# Revit family: Krill 3.4
name_source: partatom
category: Lighting Fixtures
units: mm (PartAtom-declared; Revit-internal decimal feet)

## family parameters
Always vertical = No
Cut with Voids When Loaded = No
Light Source = No
OmniClass Number = 23.80.70.00
OmniClass Title = Lighting
Part Type = Normal
Room Calculation Point = Yes
Round Connector Dimension = Use Diameter
Shared = No
Work Plane-Based = No

## types (2) — shared parameters
Apparent Load Phase 1 = 5 W
Base = L&L_Anticorodal aluminium
Base bracket = Krill 1.4_Base braket
Body = L&L_Anticorodal aluminium
CRI = CRI>90
Code = -
Control system = -
Cutout dimensions = -
Delivered lumen output = 253 lm (3000K, 350mA, 80°)
Description = Projectors for indoor applications
Energy efficiency class = A A+ A++
Features = -
Geometry = Krill 3.4_mod
H1 = 16 mm  [stored 0.0524934 ft]
IP = IP40
Joint = L&L_Brass
LED Colour = 3000K (also available: 2700, 4000K - ref. URL Technical sheet)
Length mm = 40 mm  [stored 0.131234 ft]
Lens = L&L_Tempered extra-clear glass
Lumen output at source = 452 lm (3000K, 350mA)
Manufacturer = L&L Luce&Light
Material = body in anticorodal aluminium, joint in brass
Model = Krill 3.4
Mounting = surface mounted (shop windows, display cabinets)
No. and type of led = 1 power LED High Intensity, 3-step MacAdam, 50 000h L90 B10 (Ta 25°C)
Notes = -
Power = max 4.5W
Power cables = includes 1.5 m PVC cable HT105° 2x0.20 Ø3.0 mm
Power supply = max 350mA
Power supply unit = not included
not included
not included
Trim = L&L_Black aluminium
URL = https://www.lucelight.it
URL Accessories and power supply units = https://www.lucelight.it
URL Catalogue = -
URL DXF = https://www.lucelight.it
URL Description = https://www.lucelight.it
URL General code = https://www.lucelight.it
URL IES Photometric file = https://www.lucelight.it
URL Image = https://www.lucelight.it
URL Technical sheet = https://www.lucelight.it
Vertical rotation max = 90.00°
Weight kg = 0.075 kg
Width mm = 30 mm  [stored 0.0984252 ft]
Wiring = series
X1 = 105 mm  [stored 0.344488 ft]
zero-valued in all types: Height mm

## per-type parameters (varying)
| type | Light Source | Optics |
| Krill 3.4 R1 zoom 18° (3000K 4.5W 350mA) | Light Source 3.4 : R1 zoom 18° | 18° |
| Krill 3.4 R1 zoom 80° (3000K 4.5W 350mA) | Light Source 3.4 : R1 zoom 80° | 80° |

note: [stored X ft] marks values corroborated as IEEE doubles in the binary element streams (Revit-internal decimal feet)

## geometry (parser evidence)
native form markers: Blend x2, Sweep x8
no freeform markers — native parametric forms only
